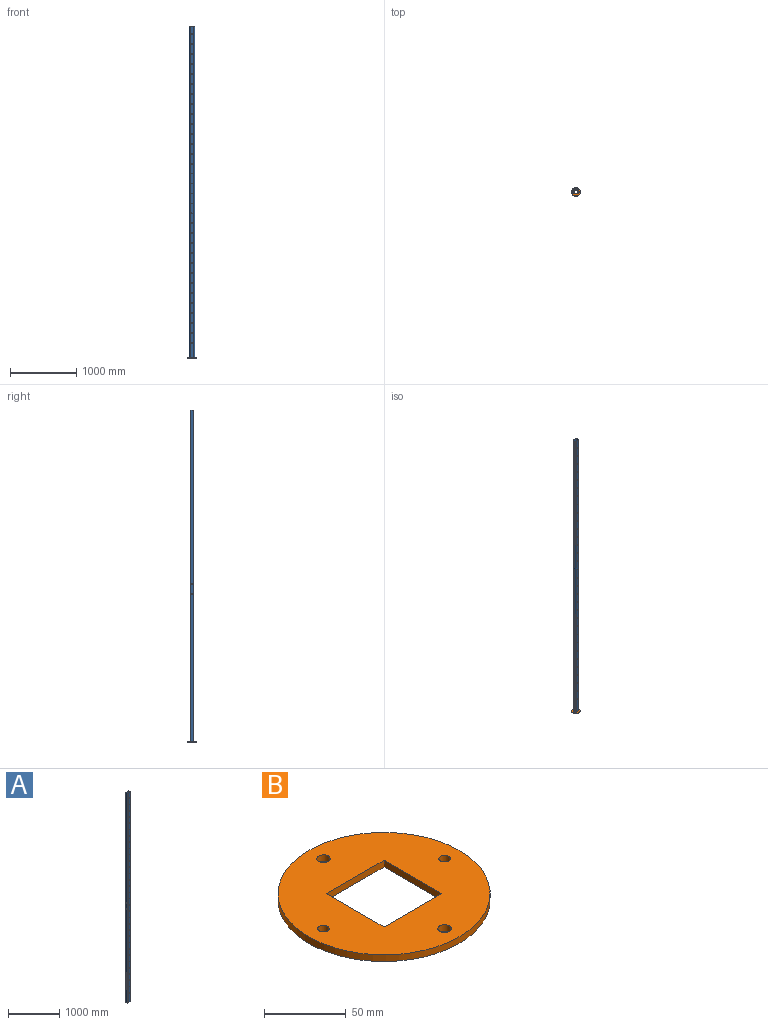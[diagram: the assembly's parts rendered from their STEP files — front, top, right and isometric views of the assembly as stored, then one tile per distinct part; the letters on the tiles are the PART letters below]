
ASSEMBLY  parts=2 mates=1
PART A: 86 faces, bbox 80x60x5000 mm
  f0: plane 5000x55mm, normal (0,-1,0), area 271259.2mm2, adj f8,f9,f10,f13,f22,f23,f24,f25
  f1: plane 5000x35mm, normal (1,0,0), area 174766.2mm2, adj f8,f9,f10,f11,f20,f21
  f2: plane 5000x55mm, normal (0,1,0), area 271259.2mm2, adj f8,f9,f11,f12,f54,f55,f56,f57
  f3: plane 5000x35mm, normal (1,0,0), area 174766.2mm2, adj f8,f9,f14,f17,f18,f19
  f4: plane 5000x55mm, normal (0,-1,0), area 271259.2mm2, adj f8,f9,f14,f15,f54,f55,f56,f57
  f5: plane 5000x35mm, normal (-1,0,0), area 174766.2mm2, adj f8,f9,f15,f16,f20,f21
  f6: plane 5000x55mm, normal (0,1,0), area 271259.2mm2, adj f8,f9,f16,f17,f22,f23,f24,f25
  f7: plane 5000x35mm, normal (-1,0,0), area 174766.2mm2, adj f8,f9,f12,f13,f18,f19
  f8: plane 80x60mm, normal (0,0,1), area 1214.2mm2, adj f0,f1,f2,f3,f4,f5,f6,f7
  f9: plane 80x60mm, normal (0,0,-1), area 1214.2mm2, adj f0,f1,f2,f3,f4,f5,f6,f7
  f10: cylinder r=12.5mm len=5000mm, axis (0,0,1), area 98174.8mm2, adj f0,f1,f8,f9
  f11: cylinder r=12.5mm len=5000mm, axis (0,0,-1), area 98174.8mm2, adj f1,f2,f8,f9
  f12: cylinder r=12.5mm len=5000mm, axis (0,0,1), area 98174.8mm2, adj f2,f7,f8,f9
  f13: cylinder r=12.5mm len=5000mm, axis (0,0,-1), area 98174.8mm2, adj f0,f7,f8,f9
  f14: cylinder r=7.5mm len=5000mm, axis (0,0,-1), area 58904.9mm2, adj f3,f4,f8,f9
  f15: cylinder r=7.5mm len=5000mm, axis (0,0,1), area 58904.9mm2, adj f4,f5,f8,f9
  f16: cylinder r=7.5mm len=5000mm, axis (0,0,-1), area 58904.9mm2, adj f5,f6,f8,f9
  f17: cylinder r=7.5mm len=5000mm, axis (0,0,1), area 58904.9mm2, adj f3,f6,f8,f9
  f18: cylinder r=6.1mm len=12.2mm, axis (1,0,0), area 191.6mm2, adj f3,f7
  f19: cylinder r=6.1mm len=12.2mm, axis (1,0,0), area 191.6mm2, adj f3,f7
  f20: cylinder r=6.1mm len=12.2mm, axis (1,0,0), area 191.6mm2, adj f1,f5
  f21: cylinder r=6.1mm len=12.2mm, axis (1,0,0), area 191.6mm2, adj f1,f5
  f22: cylinder r=6.1mm len=12.2mm, axis (0,-1,0), area 191.6mm2, adj f0,f6
  f23: cylinder r=6.1mm len=12.2mm, axis (0,-1,0), area 191.6mm2, adj f0,f6
  f24: cylinder r=6.1mm len=12.2mm, axis (0,-1,0), area 191.6mm2, adj f0,f6
  f25: cylinder r=6.1mm len=12.2mm, axis (0,-1,0), area 191.6mm2, adj f0,f6
  f26: cylinder r=6.1mm len=12.2mm, axis (0,-1,0), area 191.6mm2, adj f0,f6
  f27: cylinder r=6.1mm len=12.2mm, axis (0,-1,0), area 191.6mm2, adj f0,f6
  f28: cylinder r=6.1mm len=12.2mm, axis (0,-1,0), area 191.6mm2, adj f0,f6
  f29: cylinder r=6.1mm len=12.2mm, axis (0,-1,0), area 191.6mm2, adj f0,f6
  f30: cylinder r=6.1mm len=12.2mm, axis (0,-1,0), area 191.6mm2, adj f0,f6
  f31: cylinder r=6.1mm len=12.2mm, axis (0,-1,0), area 191.6mm2, adj f0,f6
  f32: cylinder r=6.1mm len=12.2mm, axis (0,-1,0), area 191.6mm2, adj f0,f6
  f33: cylinder r=6.1mm len=12.2mm, axis (0,-1,0), area 191.6mm2, adj f0,f6
  f34: cylinder r=6.1mm len=12.2mm, axis (0,-1,0), area 191.6mm2, adj f0,f6
  f35: cylinder r=6.1mm len=12.2mm, axis (0,-1,0), area 191.6mm2, adj f0,f6
  f36: cylinder r=6.1mm len=12.2mm, axis (0,-1,0), area 191.6mm2, adj f0,f6
  f37: cylinder r=6.1mm len=12.2mm, axis (0,-1,0), area 191.6mm2, adj f0,f6
  f38: cylinder r=6.1mm len=12.2mm, axis (0,-1,0), area 191.6mm2, adj f0,f6
  f39: cylinder r=6.1mm len=12.2mm, axis (0,-1,0), area 191.6mm2, adj f0,f6
  f40: cylinder r=6.1mm len=12.2mm, axis (0,-1,0), area 191.6mm2, adj f0,f6
  f41: cylinder r=6.1mm len=12.2mm, axis (0,-1,0), area 191.6mm2, adj f0,f6
  f42: cylinder r=6.1mm len=12.2mm, axis (0,-1,0), area 191.6mm2, adj f0,f6
  f43: cylinder r=6.1mm len=12.2mm, axis (0,-1,0), area 191.6mm2, adj f0,f6
  f44: cylinder r=6.1mm len=12.2mm, axis (0,-1,0), area 191.6mm2, adj f0,f6
  f45: cylinder r=6.1mm len=12.2mm, axis (0,-1,0), area 191.6mm2, adj f0,f6
  f46: cylinder r=6.1mm len=12.2mm, axis (0,-1,0), area 191.6mm2, adj f0,f6
  f47: cylinder r=6.1mm len=12.2mm, axis (0,-1,0), area 191.6mm2, adj f0,f6
  f48: cylinder r=6.1mm len=12.2mm, axis (0,-1,0), area 191.6mm2, adj f0,f6
  f49: cylinder r=6.1mm len=12.2mm, axis (0,-1,0), area 191.6mm2, adj f0,f6
  f50: cylinder r=6.1mm len=12.2mm, axis (0,-1,0), area 191.6mm2, adj f0,f6
  f51: cylinder r=6.1mm len=12.2mm, axis (0,-1,0), area 191.6mm2, adj f0,f6
  f52: cylinder r=6.1mm len=12.2mm, axis (0,-1,0), area 191.6mm2, adj f0,f6
  f53: cylinder r=6.1mm len=12.2mm, axis (0,-1,0), area 191.6mm2, adj f0,f6
  f54: cylinder r=6.1mm len=12.2mm, axis (0,-1,0), area 191.6mm2, adj f2,f4
  f55: cylinder r=6.1mm len=12.2mm, axis (0,-1,0), area 191.6mm2, adj f2,f4
  f56: cylinder r=6.1mm len=12.2mm, axis (0,-1,0), area 191.6mm2, adj f2,f4
  f57: cylinder r=6.1mm len=12.2mm, axis (0,-1,0), area 191.6mm2, adj f2,f4
  f58: cylinder r=6.1mm len=12.2mm, axis (0,-1,0), area 191.6mm2, adj f2,f4
  f59: cylinder r=6.1mm len=12.2mm, axis (0,-1,0), area 191.6mm2, adj f2,f4
  f60: cylinder r=6.1mm len=12.2mm, axis (0,-1,0), area 191.6mm2, adj f2,f4
  f61: cylinder r=6.1mm len=12.2mm, axis (0,-1,0), area 191.6mm2, adj f2,f4
  f62: cylinder r=6.1mm len=12.2mm, axis (0,-1,0), area 191.6mm2, adj f2,f4
  f63: cylinder r=6.1mm len=12.2mm, axis (0,-1,0), area 191.6mm2, adj f2,f4
  f64: cylinder r=6.1mm len=12.2mm, axis (0,-1,0), area 191.6mm2, adj f2,f4
  f65: cylinder r=6.1mm len=12.2mm, axis (0,-1,0), area 191.6mm2, adj f2,f4
  f66: cylinder r=6.1mm len=12.2mm, axis (0,-1,0), area 191.6mm2, adj f2,f4
  f67: cylinder r=6.1mm len=12.2mm, axis (0,-1,0), area 191.6mm2, adj f2,f4
  f68: cylinder r=6.1mm len=12.2mm, axis (0,-1,0), area 191.6mm2, adj f2,f4
  f69: cylinder r=6.1mm len=12.2mm, axis (0,-1,0), area 191.6mm2, adj f2,f4
  f70: cylinder r=6.1mm len=12.2mm, axis (0,-1,0), area 191.6mm2, adj f2,f4
  f71: cylinder r=6.1mm len=12.2mm, axis (0,-1,0), area 191.6mm2, adj f2,f4
  f72: cylinder r=6.1mm len=12.2mm, axis (0,-1,0), area 191.6mm2, adj f2,f4
  f73: cylinder r=6.1mm len=12.2mm, axis (0,-1,0), area 191.6mm2, adj f2,f4
  f74: cylinder r=6.1mm len=12.2mm, axis (0,-1,0), area 191.6mm2, adj f2,f4
  f75: cylinder r=6.1mm len=12.2mm, axis (0,-1,0), area 191.6mm2, adj f2,f4
  f76: cylinder r=6.1mm len=12.2mm, axis (0,-1,0), area 191.6mm2, adj f2,f4
  f77: cylinder r=6.1mm len=12.2mm, axis (0,-1,0), area 191.6mm2, adj f2,f4
  f78: cylinder r=6.1mm len=12.2mm, axis (0,-1,0), area 191.6mm2, adj f2,f4
  f79: cylinder r=6.1mm len=12.2mm, axis (0,-1,0), area 191.6mm2, adj f2,f4
  f80: cylinder r=6.1mm len=12.2mm, axis (0,-1,0), area 191.6mm2, adj f2,f4
  f81: cylinder r=6.1mm len=12.2mm, axis (0,-1,0), area 191.6mm2, adj f2,f4
  f82: cylinder r=6.1mm len=12.2mm, axis (0,-1,0), area 191.6mm2, adj f2,f4
  f83: cylinder r=6.1mm len=12.2mm, axis (0,-1,0), area 191.6mm2, adj f2,f4
  f84: cylinder r=6.1mm len=12.2mm, axis (0,-1,0), area 191.6mm2, adj f2,f4
  f85: cylinder r=6.1mm len=12.2mm, axis (0,-1,0), area 191.6mm2, adj f2,f4
PART B: 11 faces, bbox 130x130x5 mm
  f0: plane 50x5mm, normal (1,0,0), area 250mm2, adj f1,f7,f9,f10
  f1: plane 50x5mm, normal (0,-1,0), area 250mm2, adj f0,f2,f9,f10
  f2: plane 50x5mm, normal (-1,0,0), area 250mm2, adj f1,f7,f9,f10
  f3: cylinder r=4.1mm len=8.2mm, axis (0,0,-1), area 128.8mm2, adj f9,f10
  f4: cylinder r=4.1mm len=8.2mm, axis (0,0,-1), area 128.8mm2, adj f9,f10
  f5: cylinder r=3.5mm len=7mm, axis (0,0,-1), area 110mm2, adj f9,f10
  f6: cylinder r=3.5mm len=7mm, axis (0,0,-1), area 110mm2, adj f9,f10
  f7: plane 50x5mm, normal (0,1,0), area 250mm2, adj f0,f2,f9,f10
  f8: cylinder r=65mm len=130mm, axis (0,0,-1), area 2042mm2, adj f9,f10
  f9: plane 130x130mm, normal (0,0,1), area 10590.6mm2, adj f0,f1,f2,f3,f4,f5,f6,f7
  f10: plane 130x130mm, normal (0,0,-1), area 10590.6mm2, adj f0,f1,f2,f3,f4,f5,f6,f7
PLACE A t=(-2415.94,126.52,-562.6)mm
PLACE B t=(-2523.48,-90.62,-567.6)mm
MATE fastened B.f8 <-> A.f9  axis (0,0,1) through (-2630.75,-240.86,-562.6)mm
